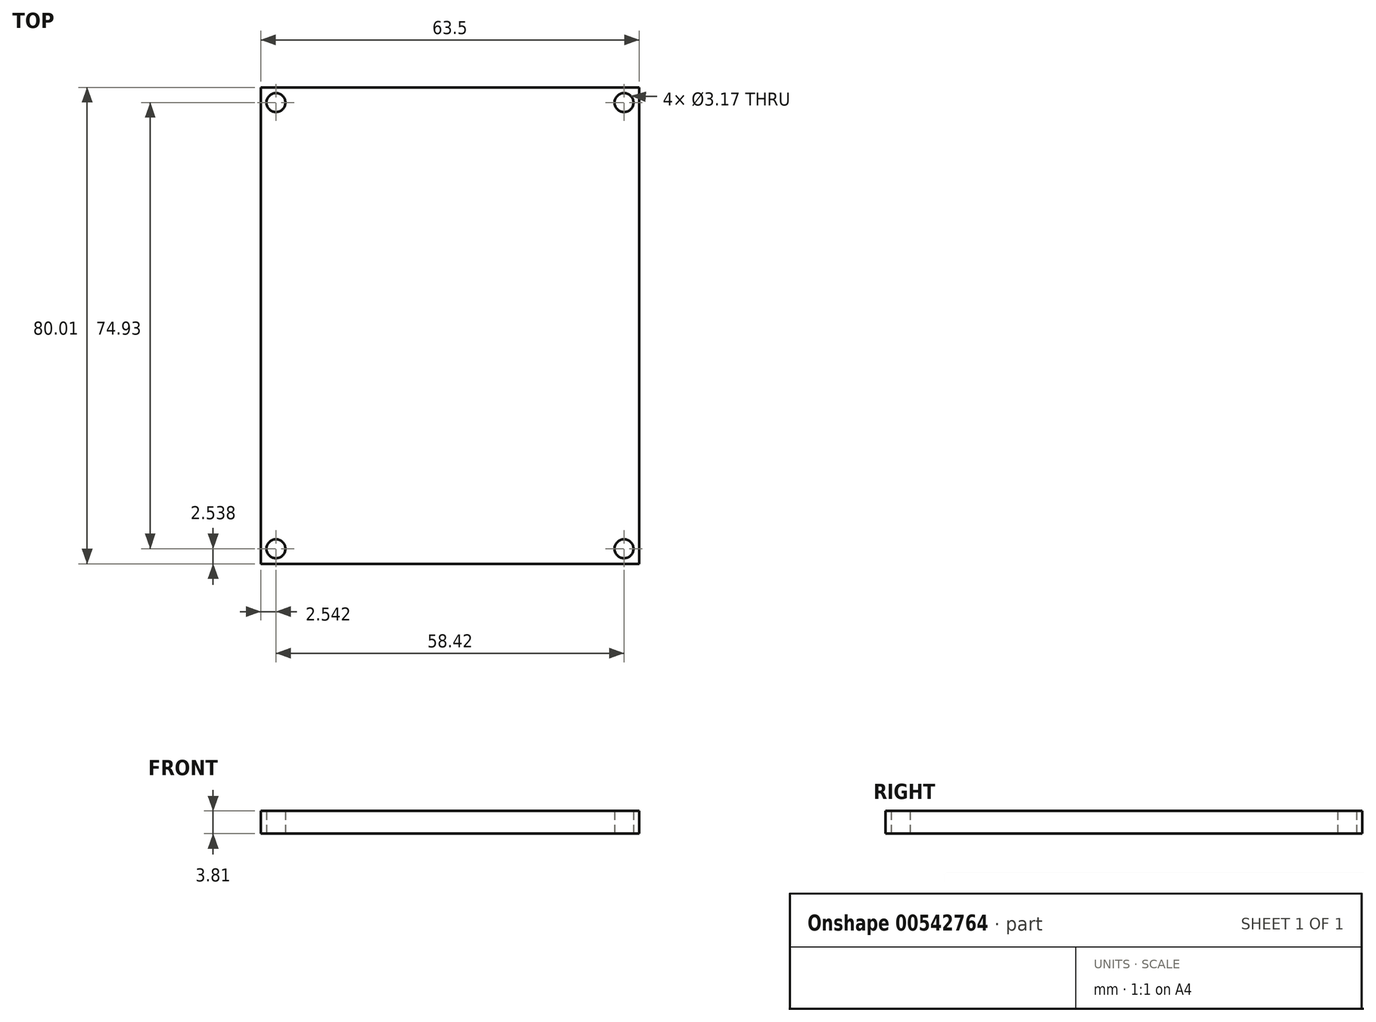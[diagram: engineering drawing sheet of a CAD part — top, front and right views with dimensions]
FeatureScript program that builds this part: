
annotation { "Feature Type Name" : "Feature", "Feature Type Description" : "" }
export const myFeature = defineFeature(function(context is Context, id is Id, definition is map)
    precondition{}
    {
        {
            var Q0;
            Q0=qCreatedBy(makeId("Top.planeOp"),FACE);
            var sketch = newSketch(context, id + "F0", { "sketchPlane" : qUnion([Q0])});
            skLineSegment(sketch, "E0.bottom", {"start": v(-33.08, 55.35) * mm, "end": v(30.42, 55.35) * mm});
            skLineSegment(sketch, "E0.top", {"start": v(-33.08, -24.66) * mm, "end": v(30.42, -24.66) * mm});
            skLineSegment(sketch, "E0.left", {"start": v(-33.08, 55.35) * mm, "end": v(-33.08, -24.66) * mm});
            skLineSegment(sketch, "E0.right", {"start": v(30.42, 55.35) * mm, "end": v(30.42, -24.66) * mm});
            skLineSegment(sketch, "E1.bottom", {"start": v(-33.08, 55.35) * mm, "end": v(-28, 55.35) * mm});
            skLineSegment(sketch, "E1.left", {"start": v(-33.08, 55.35) * mm, "end": v(-33.08, 50.27) * mm});
            skLineSegment(sketch, "E2.bottom", {"start": v(30.42, -24.66) * mm, "end": v(25.34, -24.66) * mm});
            skLineSegment(sketch, "E2.left", {"start": v(30.42, -24.66) * mm, "end": v(30.42, -19.58) * mm});
            skLineSegment(sketch, "E3.bottom", {"start": v(-28, 50.27) * mm, "end": v(25.34, 50.27) * mm});
            skLineSegment(sketch, "E3.top", {"start": v(-28, -19.58) * mm, "end": v(25.34, -19.58) * mm});
            skLineSegment(sketch, "E3.left", {"start": v(-28, 50.27) * mm, "end": v(-28, -19.58) * mm});
            skLineSegment(sketch, "E3.right", {"start": v(25.34, 50.27) * mm, "end": v(25.34, -19.58) * mm});
            skCircle(sketch, "E4", {"center": v(-30.54, 52.8) * mm, "radius": 1.59 * mm});
            skCircle(sketch, "E5.MirrorC", {"center": v(27.88, 52.8) * mm, "radius": 1.59 * mm});
            skLineSegment(sketch, "E6.MirrorCS", {"start": v(30.42, 55.35) * mm, "end": v(30.42, 50.27) * mm});
            skLineSegment(sketch, "E7.MirrorCS", {"start": v(30.42, 55.35) * mm, "end": v(25.34, 55.35) * mm});
            skCircle(sketch, "E8.MirrorC", {"center": v(-30.54, -22.12) * mm, "radius": 1.59 * mm});
            skLineSegment(sketch, "E9.MirrorCS", {"start": v(-33.08, -24.66) * mm, "end": v(-28, -24.66) * mm});
            skLineSegment(sketch, "E10.MirrorCS", {"start": v(-33.08, -24.66) * mm, "end": v(-33.08, -19.58) * mm});
            skCircle(sketch, "E11.MirrorC", {"center": v(27.88, -22.12) * mm, "radius": 1.59 * mm});
            skSolve(sketch);
        }
        {
            var Q0;
            Q0=makeQuery(id+"F0.imprint","IMPRINT",FACE,{"disambiguationData":[TD([[makeQuery(id+"F0.imprint","IMPRINT",EDGE,{"derivedFrom":sQuery(id+"F0.wireOp",EDGE,"E0.bottom")}),-1.0]])]});
            var Q1;
            Q1=makeQuery(id+"F0.imprint","IMPRINT",FACE,{"disambiguationData":[TD([[makeQuery(id+"F0.imprint","IMPRINT",EDGE,{"derivedFrom":sQuery(id+"F0.wireOp",EDGE,"E3.bottom")}),-1.0]])]});
            extrude(context, id + "F1", {"entities" : qUnion([Q0, Q1]), "depth" : 3.8 * mm, "offsetDistance" : 25.4 * mm});
        }
    });
